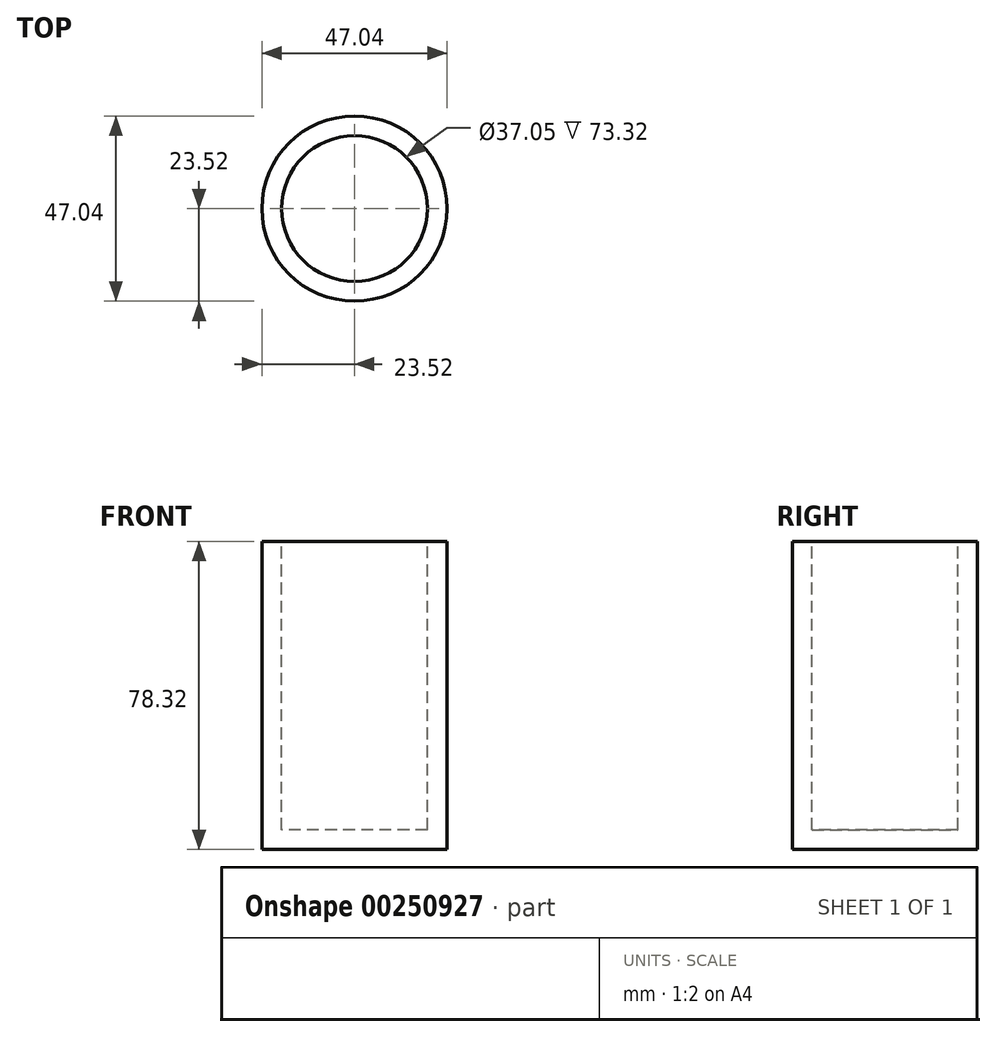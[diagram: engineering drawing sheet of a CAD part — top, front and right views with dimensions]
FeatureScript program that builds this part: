
annotation { "Feature Type Name" : "Feature", "Feature Type Description" : "" }
export const myFeature = defineFeature(function(context is Context, id is Id, definition is map)
    precondition{}
    {
        {
            var Q0;
            Q0=qCreatedBy(makeId("Front.planeOp"),FACE);
            var sketch = newSketch(context, id + "F0", { "sketchPlane" : qUnion([Q0])});
            skLineSegment(sketch, "E0.bottom", {"start": v(23.52, -39.16) * mm, "end": v(-23.52, -39.16) * mm});
            skLineSegment(sketch, "E0.top", {"start": v(23.52, 39.16) * mm, "end": v(-23.52, 39.16) * mm});
            skLineSegment(sketch, "E0.left", {"start": v(23.52, -39.16) * mm, "end": v(23.52, 39.16) * mm});
            skLineSegment(sketch, "E0.right", {"start": v(-23.52, -39.16) * mm, "end": v(-23.52, 39.16) * mm});
            skPoint(sketch, "E0.middle", {"position": v(0, 0) * mm});
            skLineSegment(sketch, "E1", {"start": v(0, 39.16) * mm, "end": v(0, -39.16) * mm});
            skSolve(sketch);
        }
        {
            var Q0;
            {var subQ0=sQuery(id+"F0.wireOp",EDGE,"E0.right");Q0=makeQuery(id+"F0.imprint","IMPRINT",FACE,{"disambiguationData":[TD([[makeQuery(id+"F0.imprint","IMPRINT",EDGE,{"derivedFrom":subQ0}),-1.0]])]});}
            var Q1;
            Q1=sQuery(id+"F0.wireOp",EDGE,"E1");
            revolve(context, id + "F1", {"entities" : qUnion([Q0]), "axis" : qUnion([Q1]), "revolveType" : RevolveType.FULL});
        }
        {
            var Q0;
            Q0=makeQuery(id+"F1.opRevolve","SWEPT_FACE",FACE,{"disambiguationData":[OSD([sQuery(id+"F0.wireOp",EDGE,"E0.top")])]});
            shell(context, id + "F2", {"entities" : qUnion([Q0]), "thickness" : 5 * mm});
        }
    });
